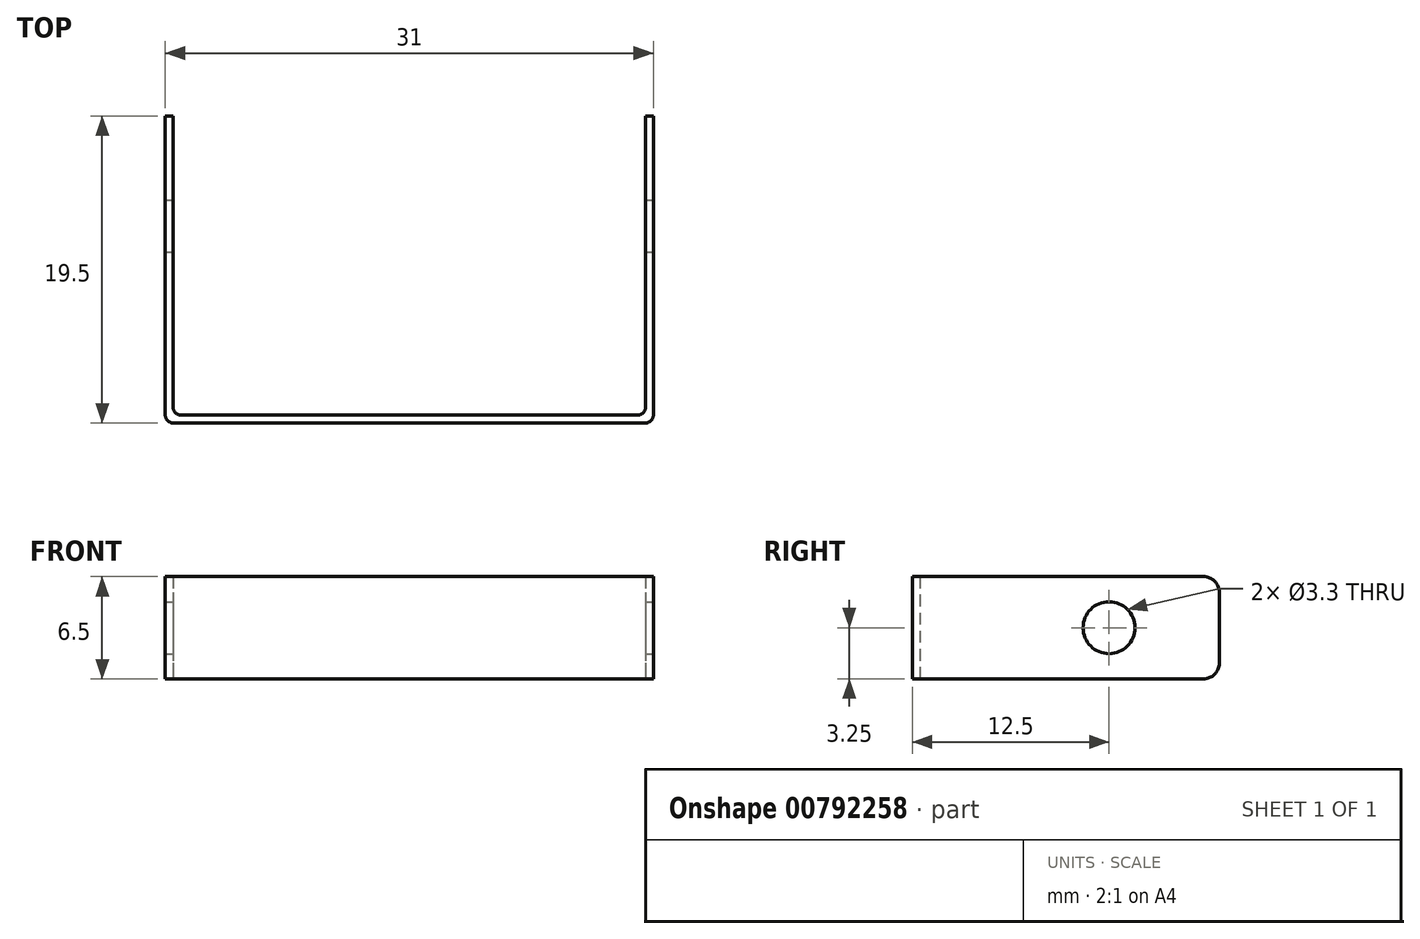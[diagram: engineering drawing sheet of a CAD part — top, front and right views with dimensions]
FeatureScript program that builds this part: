
annotation { "Feature Type Name" : "Feature", "Feature Type Description" : "" }
export const myFeature = defineFeature(function(context is Context, id is Id, definition is map)
    precondition{}
    {
        {
            var Q0;
            Q0=qCreatedBy(makeId("Top.planeOp"),FACE);
            var sketch = newSketch(context, id + "F0", { "sketchPlane" : qUnion([Q0])});
            skLineSegment(sketch, "E0", {"start": v(-15, 0) * mm, "end": v(15, 0) * mm});
            skLineSegment(sketch, "E1", {"start": v(15, 0) * mm, "end": v(15, 19) * mm});
            skLineSegment(sketch, "E2", {"start": v(-15, 0) * mm, "end": v(-15, 19) * mm});
            skLineSegment(sketch, "E3.0", {"start": v(-15.5, -0.5) * mm, "end": v(-15.5, 19) * mm});
            skLineSegment(sketch, "E3.1", {"start": v(-15.5, -0.5) * mm, "end": v(15.5, -0.5) * mm});
            skLineSegment(sketch, "E3.2", {"start": v(15.5, -0.5) * mm, "end": v(15.5, 19) * mm});
            skLineSegment(sketch, "E4", {"start": v(-15.5, 19) * mm, "end": v(-15, 19) * mm});
            skLineSegment(sketch, "E5", {"start": v(15.5, 19) * mm, "end": v(15, 19) * mm});
            skSolve(sketch);
        }
        {
            var Q0;
            Q0 = qSketchRegion(id + "F0", true);
            extrude(context, id + "F1", {"entities" : qUnion([Q0]), "depth" : 6.5 * mm, "offsetDistance" : 25 * mm});
        }
        {
            var Q0;
            Q0=makeQuery(id+"F1.opExtrude","SWEPT_FACE",FACE,{"disambiguationData":[OSD([sQuery(id+"F0.wireOp",EDGE,"E3.2")])]});
            var sketch = newSketch(context, id + "F2", { "sketchPlane" : qUnion([Q0])});
            skCircle(sketch, "E6", {"center": v(12, 3.25) * mm, "radius": 1.65 * mm});
            skSolve(sketch);
        }
        {
            var Q0;
            Q0 = qSketchRegion(id + "F2", true);
            extrude(context, id + "F3", {"entities" : qUnion([Q0]), "operationType" : NewBodyOperationType.REMOVE, "endBound" : BoundingType.THROUGH_ALL, "oppositeDirection" : true, "depth" : 25 * mm, "offsetDistance" : 25 * mm});
        }
        {
            var Q0;
            Q0=makeQuery(id+"F1.opExtrude","SWEPT_EDGE",EDGE,{"disambiguationData":[OSD([sQuery(id+"F0.wireOp",EDGE,"E3.0"),sQuery(id+"F0.wireOp",EDGE,"E3.1")])]});
            var Q1;
            Q1=makeQuery(id+"F1.opExtrude","SWEPT_EDGE",EDGE,{"disambiguationData":[OSD([sQuery(id+"F0.wireOp",EDGE,"E3.1"),sQuery(id+"F0.wireOp",EDGE,"E3.2")])]});
            var Q2;
            Q2=makeQuery(id+"F1.opExtrude","SWEPT_EDGE",EDGE,{"disambiguationData":[OSD([sQuery(id+"F0.wireOp",EDGE,"E0"),sQuery(id+"F0.wireOp",EDGE,"E1")])]});
            var Q3;
            Q3=makeQuery(id+"F1.opExtrude","SWEPT_EDGE",EDGE,{"disambiguationData":[OSD([sQuery(id+"F0.wireOp",EDGE,"E0"),sQuery(id+"F0.wireOp",EDGE,"E2")])]});
            fillet(context, id + "F4", {"entities" : qUnion([Q0, Q1, Q2, Q3]), "radius" : 0.5 * mm, "tangentPropagation" : true, "allowEdgeOverflow" : false});
        }
        {
            var Q0;
            Q0=makeQuery(id+"F1.opExtrude","CAP_EDGE",EDGE,{"disambiguationData":[OSD([sQuery(id+"F0.wireOp",EDGE,"E4")])],"isStart":false});
            var Q1;
            Q1=makeQuery(id+"F1.opExtrude","CAP_EDGE",EDGE,{"disambiguationData":[OSD([sQuery(id+"F0.wireOp",EDGE,"E4")])],"isStart":true});
            var Q2;
            Q2=makeQuery(id+"F1.opExtrude","CAP_EDGE",EDGE,{"disambiguationData":[OSD([sQuery(id+"F0.wireOp",EDGE,"E5")])],"isStart":false});
            var Q3;
            Q3=makeQuery(id+"F1.opExtrude","CAP_EDGE",EDGE,{"disambiguationData":[OSD([sQuery(id+"F0.wireOp",EDGE,"E5")])],"isStart":true});
            fillet(context, id + "F5", {"entities" : qUnion([Q0, Q1, Q2, Q3]), "radius" : 1 * mm, "tangentPropagation" : true, "allowEdgeOverflow" : false});
        }
    });
